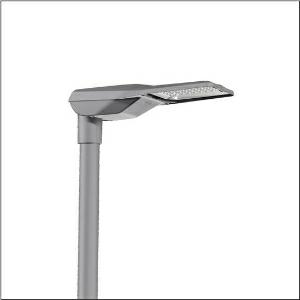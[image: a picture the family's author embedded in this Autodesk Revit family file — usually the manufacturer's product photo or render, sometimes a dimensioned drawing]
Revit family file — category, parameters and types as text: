
# Revit family: streetlight_sl_21_iq_mini___st0_5a_5xe2b31d08jb_7d26
name_source: partatom
category: Lighting Fixtures
units: mm (PartAtom-declared; Revit-internal decimal feet)

## family parameters
Cut with Voids When Loaded = No
Host = Face
Light Source = No
Part Type = Normal
Room Calculation Point = No
Round Connector Dimension = Use Diameter
Shared = No

## types (1)
- --- (1 x LED, 10820 lm, 71.6 W, 3000K)
    Apparent Load = 72 VA
    CIE Flux Codes = 43 76 97 100 100
    Color Rendering = 70
    Color Temperature = 3000K
    Default Elevation = 1800 mm
    Description = Streetlight SL 21 iQ mini, mast luminaire, primary light control with lens, of PMMA, primary optical cover: cover, of toughened safety glass, transparent, light distribution: ST0.5a, light emission: direct distribution, primary light characteristic: asymmetric, installation type: post-top, side-entry, LED, High Power LED, rated luminous flux: 10.820lm, luminous efficacy: 151lm/W, light colour: 730, colour temperature: 3000K, control gear: iQ-Comfort, control: Auto-Match, Temp-Guard, Lumen-Switch, Night-Set, Smart-Wire, Light-Fading, Desk-Remote (wireless, voltage-free reading and setting of iQ features in the workshop via application-optimized NFC function/RFID function), optimised constant luminous flux control (CLO 2.0), pre-setting: linear dimming characteristic, mains connection: 220..240V, AC, 50/60Hz, start of lifetime: 72W, end of service life: 75W, reduction: 33W, luminaire housing, of diecast aluminium, powder-coated, SITECO metallic grey (DB 702S), corrosivity category C5 high according to DIN EN ISO 12944, please order mast flange separately, inclination adjustable: 0°, 5°, 10°, 15°, sealing non-destructively replaceable, multi-level sealing system, length: 628mm, width: 235mm, height: 110mm, mast flange for spigot size: 42mm (side-entry): 5XC10008XM4, 60/48mm (side-entry/post-top): 5XC10108XM2, 76/60mm (side-entry/post-top): 5XC10108XM1, mounting height: 4..8m, protection rating (complete): IP66, insulation class (complete): insulation class II (safety insulation), certification: CE, ENEC, ENEC+, VDE, impact resistance: IK10, permissible operating ambient temperature for outdoor applications: -40..+50°C, standard-compliant lighting for roads and squares, packaging unit: 1 piece

Light Distribution: ST0.5a
    Height = 110 mm
    Lamp = 1 x LED
    Lamp Light Flux = 10820 lm
    Lamp Power = 71.6 W
    Lamp count = 1
    Length = 625 mm
    Luminous efficacy = 151 lm/W
    Manufacturer = Siteco
    ModVariant = No
    Model = 5XE2B31D08JB
    Number of Poles = 1
    OnlyDefault = Yes
    Power Factor = 1
    Product Name = Streetlight SL 21 iQ mini | ST0.5a
    Product group = mast luminaire | pylon top
    ProductGroupID = 6100
    Protection Class = Protection class II
    Protection Degree = IP 66
    RLX_Detail_Level = 1
    RLX_Emergency_Light_Flux = 0 lm
    RLX_Emergency_Type = 0
    RLX_Emergency_Type_DB = No
    RlxData = <blob elided: 37493 chars, md5=cbbf465e>
    Socket = socket
    Standby Power = 0 W
    System Light Flux = 10820 lm
    System Power = 72 W
    Type Comments = factory setting: luminous flux: 100 % | dim-lin: 254 | 746 mA
    Type Image = l_1003519.jpg
    URL = http://relux.com
    VarID = @adj_171293
    Voltage = 0 V
    Weight = 0.00 kg
    Width = 234 mm

## geometry (parser evidence)
native form markers: Blend x4, Sweep x11
no freeform markers — native parametric forms only
